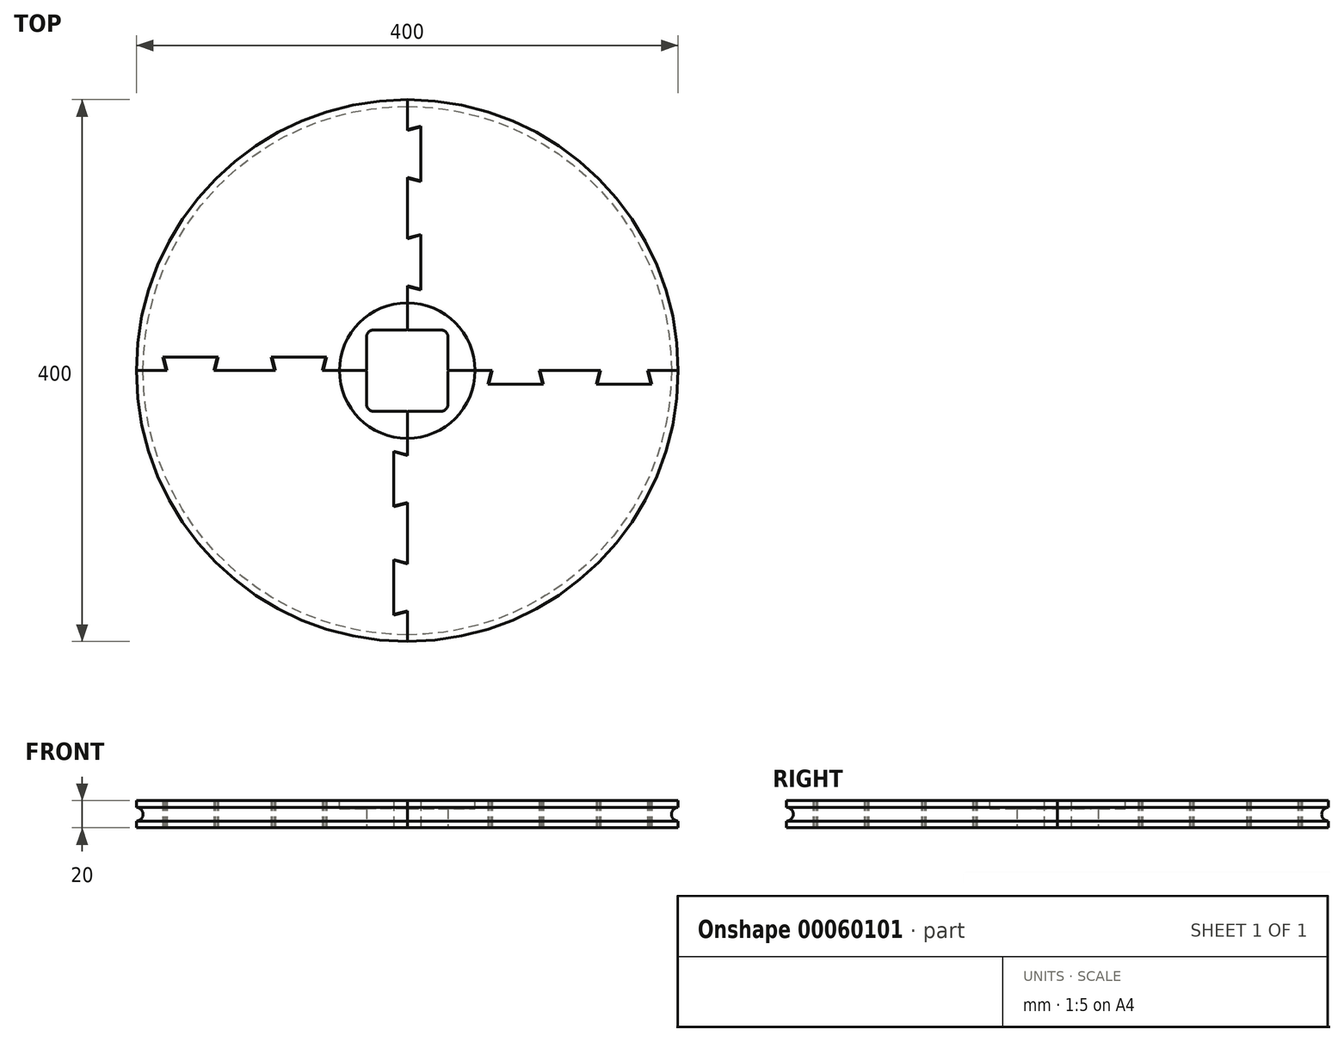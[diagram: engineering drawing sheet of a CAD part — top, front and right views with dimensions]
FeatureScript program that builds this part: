
annotation { "Feature Type Name" : "Feature", "Feature Type Description" : "" }
export const myFeature = defineFeature(function(context is Context, id is Id, definition is map)
    precondition{}
    {
        {
            var Q0;
            Q0=qCreatedBy(makeId("Top.planeOp"),FACE);
            var sketch = newSketch(context, id + "F0", { "sketchPlane" : qUnion([Q0])});
            skCircle(sketch, "E0", {"center": v(0, 0) * mm, "radius": 200 * mm});
            skLineSegment(sketch, "E1.rect.bottom", {"start": v(105, 148.5) * mm, "end": v(-105, 148.5) * mm, "construction": true});
            skLineSegment(sketch, "E1.rect.top", {"start": v(105, -148.5) * mm, "end": v(-105, -148.5) * mm, "construction": true});
            skLineSegment(sketch, "E1.rect.left", {"start": v(105, 148.5) * mm, "end": v(105, -148.5) * mm, "construction": true});
            skLineSegment(sketch, "E1.rect.right", {"start": v(-105, 148.5) * mm, "end": v(-105, -148.5) * mm, "construction": true});
            skLineSegment(sketch, "E2.bottom", {"start": v(0, -10) * mm, "end": v(200, -10) * mm, "construction": true});
            skLineSegment(sketch, "E2.top", {"start": v(0, 200) * mm, "end": v(200, 200) * mm, "construction": true});
            skLineSegment(sketch, "E2.left", {"start": v(0, -10) * mm, "end": v(0, 200) * mm, "construction": true});
            skLineSegment(sketch, "E2.right", {"start": v(200, -10) * mm, "end": v(200, 200) * mm, "construction": true});
            skLineSegment(sketch, "E3.bottom", {"start": v(-200, -200) * mm, "end": v(0, -200) * mm, "construction": true});
            skLineSegment(sketch, "E3.top", {"start": v(-200, 10) * mm, "end": v(0, 10) * mm, "construction": true});
            skLineSegment(sketch, "E3.left", {"start": v(-200, -200) * mm, "end": v(-200, 10) * mm, "construction": true});
            skLineSegment(sketch, "E3.right", {"start": v(0, -200) * mm, "end": v(0, 10) * mm, "construction": true});
            skLineSegment(sketch, "E4.bottom", {"start": v(-10, -200) * mm, "end": v(200, -200) * mm, "construction": true});
            skLineSegment(sketch, "E4.top", {"start": v(-10, 0) * mm, "end": v(200, 0) * mm, "construction": true});
            skLineSegment(sketch, "E4.left", {"start": v(-10, -200) * mm, "end": v(-10, 0) * mm, "construction": true});
            skLineSegment(sketch, "E4.right", {"start": v(200, -200) * mm, "end": v(200, 0) * mm, "construction": true});
            skLineSegment(sketch, "E5.bottom", {"start": v(-200, 200) * mm, "end": v(10, 200) * mm, "construction": true});
            skLineSegment(sketch, "E5.top", {"start": v(-200, 0) * mm, "end": v(10, 0) * mm, "construction": true});
            skLineSegment(sketch, "E5.left", {"start": v(-200, 200) * mm, "end": v(-200, 0) * mm, "construction": true});
            skLineSegment(sketch, "E5.right", {"start": v(10, 200) * mm, "end": v(10, 0) * mm, "construction": true});
            skLineSegment(sketch, "E6", {"start": v(0, 200) * mm, "end": v(0, 177.82) * mm});
            skLineSegment(sketch, "E7", {"start": v(0, 177.82) * mm, "end": v(10, 180.5) * mm});
            skLineSegment(sketch, "E8", {"start": v(10, 180.5) * mm, "end": v(10, 139.5) * mm});
            skLineSegment(sketch, "E9", {"start": v(10, 139.5) * mm, "end": v(0, 142.18) * mm});
            skLineSegment(sketch, "E10", {"start": v(0, 142.18) * mm, "end": v(0, 97.82) * mm});
            skLineSegment(sketch, "E11", {"start": v(0, 97.82) * mm, "end": v(10, 100.5) * mm});
            skLineSegment(sketch, "E12", {"start": v(10, 100.5) * mm, "end": v(10, 59.5) * mm});
            skLineSegment(sketch, "E13", {"start": v(10, 59.5) * mm, "end": v(0, 62.18) * mm});
            skLineSegment(sketch, "E14", {"start": v(0, 62.18) * mm, "end": v(0, 0) * mm});
            skLineSegment(sketch, "E15", {"start": v(10, 80) * mm, "end": v(0, 80) * mm, "construction": true});
            skLineSegment(sketch, "E16", {"start": v(10, 160) * mm, "end": v(0, 160) * mm, "construction": true});
            skLineSegment(sketch, "E17", {"start": v(0, 0) * mm, "end": v(62.68, 0) * mm});
            skLineSegment(sketch, "E18", {"start": v(62.68, 0) * mm, "end": v(60, -10) * mm});
            skLineSegment(sketch, "E19", {"start": v(60, -10) * mm, "end": v(100, -10) * mm});
            skLineSegment(sketch, "E20", {"start": v(100, -10) * mm, "end": v(97.32, 0) * mm});
            skLineSegment(sketch, "E21", {"start": v(97.32, 0) * mm, "end": v(142.68, 0) * mm});
            skLineSegment(sketch, "E22", {"start": v(142.68, 0) * mm, "end": v(140, -10) * mm});
            skLineSegment(sketch, "E23", {"start": v(140, -10) * mm, "end": v(180, -10) * mm});
            skLineSegment(sketch, "E24", {"start": v(180, -10) * mm, "end": v(177.32, 0) * mm});
            skLineSegment(sketch, "E25", {"start": v(177.32, 0) * mm, "end": v(200, 0) * mm});
            skLineSegment(sketch, "E26", {"start": v(80, -10) * mm, "end": v(80, 0) * mm, "construction": true});
            skLineSegment(sketch, "E27", {"start": v(160, -10) * mm, "end": v(160, 0) * mm, "construction": true});
            skLineSegment(sketch, "E28.bottom", {"start": v(0, 0) * mm, "end": v(30, 0) * mm});
            skLineSegment(sketch, "E28.top", {"start": v(0, 30) * mm, "end": v(30, 30) * mm});
            skLineSegment(sketch, "E28.left", {"start": v(0, 0) * mm, "end": v(0, 30) * mm});
            skLineSegment(sketch, "E28.right", {"start": v(30, 0) * mm, "end": v(30, 30) * mm});
            skSolve(sketch);
        }
        {
            var Q0;
            {var subQ0=sQuery(id+"F0.wireOp",EDGE,"E6");Q0=makeQuery(id+"F0.imprint","IMPRINT",FACE,{"disambiguationData":[TD([[makeQuery(id+"F0.imprint","IMPRINT",EDGE,{"derivedFrom":subQ0}),1.0]])]});}
            extrude(context, id + "F1", {"entities" : qUnion([Q0]), "endBound" : BoundingType.SYMMETRIC, "depth" : 20 * mm});
        }
        {
            var Q0;
            Q0=qCreatedBy(makeId("Front.planeOp"),FACE);
            var sketch = newSketch(context, id + "F2", { "sketchPlane" : qUnion([Q0])});
            skCircle(sketch, "E29", {"center": v(200, 0) * mm, "radius": 5 * mm});
            skSolve(sketch);
        }
        {
            var Q0;
            Q0=qCreatedBy(makeId("Front.planeOp"),FACE);
            var sketch = newSketch(context, id + "F3", { "sketchPlane" : qUnion([Q0])});
            skLineSegment(sketch, "E30", {"start": v(0, 0) * mm, "end": v(0, 27.77) * mm});
            skSolve(sketch);
        }
        {
            var Q0;
            Q0 = qSketchRegion(id + "F2", true);
            var Q1;
            Q1=sQuery(id+"F3.wireOp",EDGE,"E30");
            revolve(context, id + "F4", {"operationType" : NewBodyOperationType.REMOVE, "entities" : qUnion([Q0]), "axis" : qUnion([Q1]), "revolveType" : RevolveType.FULL, "oppositeDirection" : true});
        }
        {
            var Q0;
            Q0=makeQuery(id+"F1.opExtrude","SWEPT_EDGE",EDGE,{"disambiguationData":[OSD([sQuery(id+"F0.wireOp",EDGE,"E18"),sQuery(id+"F0.wireOp",EDGE,"E19")])]});
            var Q1;
            Q1=makeQuery(id+"F1.opExtrude","SWEPT_EDGE",EDGE,{"disambiguationData":[OSD([sQuery(id+"F0.wireOp",EDGE,"E19"),sQuery(id+"F0.wireOp",EDGE,"E20")])]});
            var Q2;
            Q2=makeQuery(id+"F1.opExtrude","SWEPT_EDGE",EDGE,{"disambiguationData":[OSD([sQuery(id+"F0.wireOp",EDGE,"E22"),sQuery(id+"F0.wireOp",EDGE,"E23")])]});
            var Q3;
            Q3=makeQuery(id+"F1.opExtrude","SWEPT_EDGE",EDGE,{"disambiguationData":[OSD([sQuery(id+"F0.wireOp",EDGE,"E23"),sQuery(id+"F0.wireOp",EDGE,"E24")])]});
            var Q4;
            Q4=makeQuery(id+"F1.opExtrude","SWEPT_EDGE",EDGE,{"disambiguationData":[OSD([sQuery(id+"F0.wireOp",EDGE,"E6"),sQuery(id+"F0.wireOp",EDGE,"E7")])]});
            var Q5;
            Q5=makeQuery(id+"F1.opExtrude","SWEPT_EDGE",EDGE,{"disambiguationData":[OSD([sQuery(id+"F0.wireOp",EDGE,"E10"),sQuery(id+"F0.wireOp",EDGE,"E11")])]});
            var Q6;
            Q6=makeQuery(id+"F1.opExtrude","SWEPT_EDGE",EDGE,{"disambiguationData":[OSD([sQuery(id+"F0.wireOp",EDGE,"E9"),sQuery(id+"F0.wireOp",EDGE,"E10")])]});
            var Q7;
            Q7=makeQuery(id+"F1.opExtrude","SWEPT_EDGE",EDGE,{"disambiguationData":[OSD([sQuery(id+"F0.wireOp",EDGE,"E13"),sQuery(id+"F0.wireOp",EDGE,"E14")])]});
            var Q8;
            Q8=makeQuery(id+"F1.opExtrude","SWEPT_EDGE",EDGE,{"disambiguationData":[OSD([sQuery(id+"F0.wireOp",EDGE,"E14"),sQuery(id+"F0.wireOp",EDGE,"E28.top"),sQuery(id+"F0.wireOp",EDGE,"E28.left")])]});
            var Q9;
            Q9=makeQuery(id+"F1.opExtrude","SWEPT_EDGE",EDGE,{"disambiguationData":[OSD([sQuery(id+"F0.wireOp",EDGE,"E17"),sQuery(id+"F0.wireOp",EDGE,"E28.bottom"),sQuery(id+"F0.wireOp",EDGE,"E28.right")])]});
            fillet(context, id + "F5", {"entities" : qUnion([Q0, Q1, Q2, Q3, Q4, Q5, Q6, Q7, Q8, Q9]), "radius" : 1 * mm, "tangentPropagation" : true, "allowEdgeOverflow" : false});
        }
        {
            var Q0;
            Q0=makeQuery(id+"F1.opExtrude","SWEPT_EDGE",EDGE,{"disambiguationData":[OSD([sQuery(id+"F0.wireOp",EDGE,"E28.top"),sQuery(id+"F0.wireOp",EDGE,"E28.right")])]});
            fillet(context, id + "F6", {"entities" : qUnion([Q0]), "radius" : 5 * mm, "tangentPropagation" : true, "allowEdgeOverflow" : false});
        }
        {
            var Q0;
            Q0=makeQuery(id+"F1.opExtrude","CAP_FACE",FACE,{"disambiguationData":[OSD([sQuery(id+"F0.wireOp",EDGE,"E0"),sQuery(id+"F0.wireOp",EDGE,"E6"),sQuery(id+"F0.wireOp",EDGE,"E7"),sQuery(id+"F0.wireOp",EDGE,"E8"),sQuery(id+"F0.wireOp",EDGE,"E9"),sQuery(id+"F0.wireOp",EDGE,"E10"),sQuery(id+"F0.wireOp",EDGE,"E11"),sQuery(id+"F0.wireOp",EDGE,"E12"),sQuery(id+"F0.wireOp",EDGE,"E13"),sQuery(id+"F0.wireOp",EDGE,"E14"),sQuery(id+"F0.wireOp",EDGE,"E17"),sQuery(id+"F0.wireOp",EDGE,"E18"),sQuery(id+"F0.wireOp",EDGE,"E19"),sQuery(id+"F0.wireOp",EDGE,"E20"),sQuery(id+"F0.wireOp",EDGE,"E21"),sQuery(id+"F0.wireOp",EDGE,"E22"),sQuery(id+"F0.wireOp",EDGE,"E23"),sQuery(id+"F0.wireOp",EDGE,"E24"),sQuery(id+"F0.wireOp",EDGE,"E25"),sQuery(id+"F0.wireOp",EDGE,"E28.top"),sQuery(id+"F0.wireOp",EDGE,"E28.right")])],"isStart":false});
            var sketch = newSketch(context, id + "F7", { "sketchPlane" : qUnion([Q0])});
            skCircle(sketch, "E31", {"center": v(0, 0) * mm, "radius": 50 * mm});
            skSolve(sketch);
        }
        {
            var Q0;
            {var subQ1=sQuery(id+"F0.wireOp",EDGE,"E28.top");Q0=makeQuery(id+"F7.imprint","IMPRINT",FACE,{"disambiguationData":[TD([[makeQuery(id+"F7.imprint","IMPRINT",EDGE,{"derivedFrom":makeQuery(id+"F1.opExtrude","CAP_EDGE",EDGE,{"disambiguationData":[OSD([subQ1])],"isStart":false})}),1.0]])]});}
            extrude(context, id + "F8", {"entities" : qUnion([Q0]), "operationType" : NewBodyOperationType.REMOVE, "oppositeDirection" : true, "depth" : 6 * mm});
        }
        {
            var Q0;
            Q0=makeQuery(id+"F1.opExtrude","SWEPT_BODY",BODY,{"disambiguationData":[OSD([sQuery(id+"F0.wireOp",EDGE,"E0"),sQuery(id+"F0.wireOp",EDGE,"E6"),sQuery(id+"F0.wireOp",EDGE,"E7"),sQuery(id+"F0.wireOp",EDGE,"E8"),sQuery(id+"F0.wireOp",EDGE,"E9"),sQuery(id+"F0.wireOp",EDGE,"E10"),sQuery(id+"F0.wireOp",EDGE,"E11"),sQuery(id+"F0.wireOp",EDGE,"E12"),sQuery(id+"F0.wireOp",EDGE,"E13"),sQuery(id+"F0.wireOp",EDGE,"E14"),sQuery(id+"F0.wireOp",EDGE,"E17"),sQuery(id+"F0.wireOp",EDGE,"E18"),sQuery(id+"F0.wireOp",EDGE,"E19"),sQuery(id+"F0.wireOp",EDGE,"E20"),sQuery(id+"F0.wireOp",EDGE,"E21"),sQuery(id+"F0.wireOp",EDGE,"E22"),sQuery(id+"F0.wireOp",EDGE,"E23"),sQuery(id+"F0.wireOp",EDGE,"E24"),sQuery(id+"F0.wireOp",EDGE,"E25"),sQuery(id+"F0.wireOp",EDGE,"E28.top"),sQuery(id+"F0.wireOp",EDGE,"E28.right")])]});
            var Q1;
            Q1=sQuery(id+"F3.wireOp",EDGE,"E30");
            circularPattern(context, id + "F9", {"entities" : qUnion([Q0]), "axis" : qUnion([Q1]), "angle" : 360 * degree, "instanceCount" : 4, "equalSpace" : true});
        }
    });
